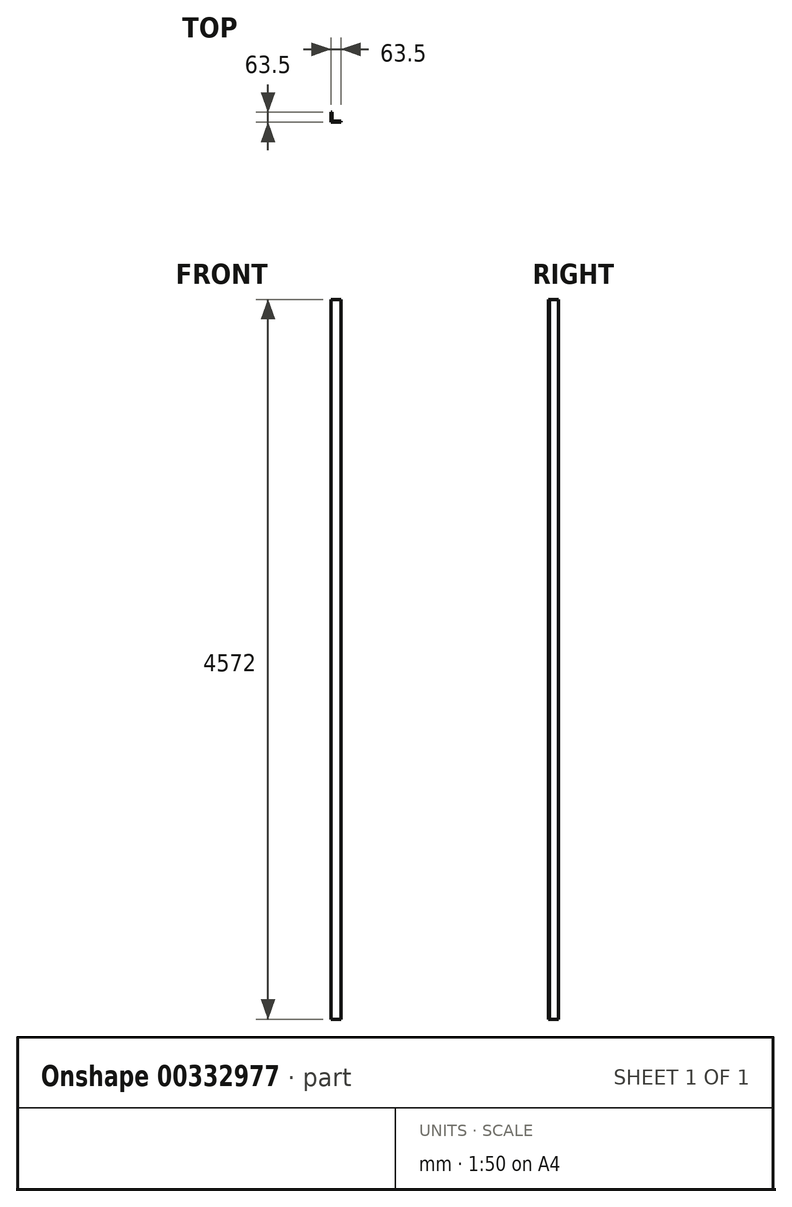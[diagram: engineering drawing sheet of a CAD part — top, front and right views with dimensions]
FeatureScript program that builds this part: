
annotation { "Feature Type Name" : "Feature", "Feature Type Description" : "" }
export const myFeature = defineFeature(function(context is Context, id is Id, definition is map)
    precondition{}
    {
        {
            var Q0;
            Q0=qCreatedBy(makeId("Top.planeOp"),FACE);
            var sketch = newSketch(context, id + "F0", { "sketchPlane" : qUnion([Q0])});
            skLineSegment(sketch, "E0", {"start": v(0, 0) * mm, "end": v(0, -63.5) * mm});
            skLineSegment(sketch, "E1", {"start": v(0, -63.5) * mm, "end": v(63.5, -63.5) * mm});
            skLineSegment(sketch, "E2", {"start": v(63.5, -63.5) * mm, "end": v(63.5, -57.15) * mm});
            skLineSegment(sketch, "E3", {"start": v(63.5, -57.15) * mm, "end": v(6.35, -57.15) * mm});
            skLineSegment(sketch, "E4", {"start": v(6.35, -57.15) * mm, "end": v(6.35, 0) * mm});
            skLineSegment(sketch, "E5", {"start": v(6.35, 0) * mm, "end": v(0, 0) * mm});
            skSolve(sketch);
        }
        {
            var Q0;
            Q0=makeQuery(id+"F0.imprint","IMPRINT",FACE,{"disambiguationData":[TD([[makeQuery(id+"F0.imprint","IMPRINT",EDGE,{"derivedFrom":sQuery(id+"F0.wireOp",EDGE,"E0")}),1.0]])]});
            extrude(context, id + "F1", {"entities" : qUnion([Q0]), "oppositeDirection" : true, "depth" : 4572 * mm});
        }
    });
